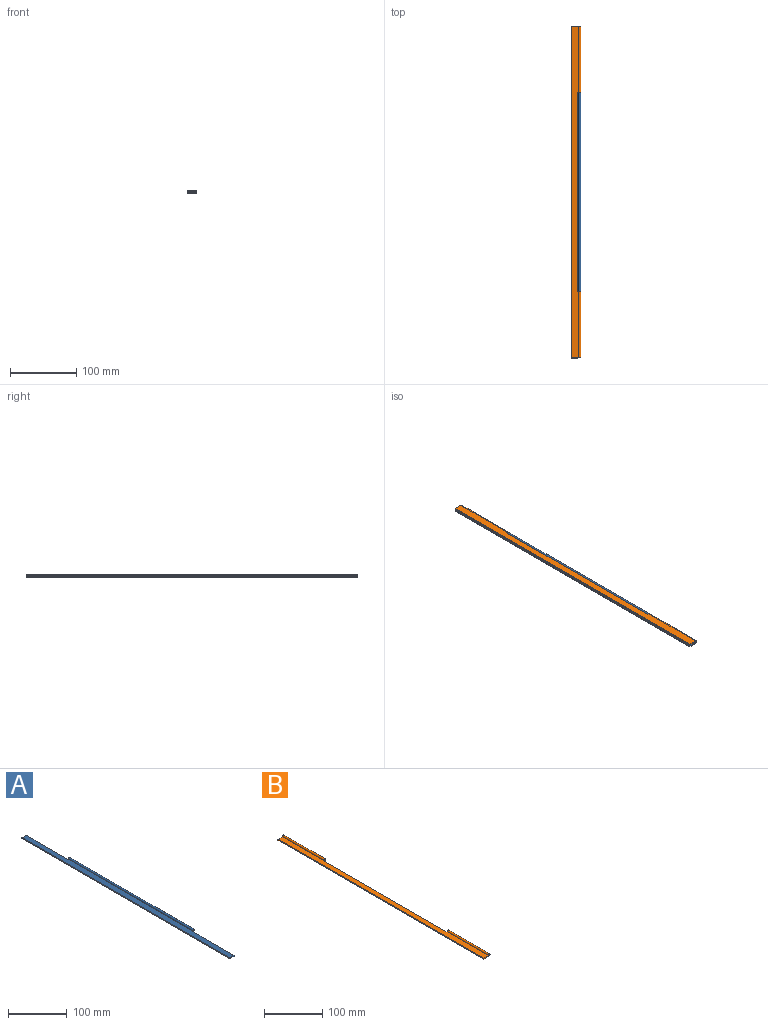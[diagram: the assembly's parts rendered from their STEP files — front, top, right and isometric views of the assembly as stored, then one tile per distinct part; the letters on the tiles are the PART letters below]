
ASSEMBLY  parts=2 mates=1
PART A: 12 faces, bbox 15x500x4.6 mm
  f0: plane 500x11.98mm, normal (0,0,-1), area 5594.8mm2, adj f1,f4,f5,f6,f7,f8,f9,f10
  f1: plane 300x0.84mm, normal (1,0,0), area 251.9mm2, adj f0,f2,f7,f9
  f2: cylinder r=2mm len=300mm, axis (0,1,0), area 3318.4mm2, adj f1,f3,f7,f9
  f3: plane 500x11.08mm, normal (0,0,1), area 5324.1mm2, adj f2,f4,f5,f6,f7,f8,f9,f10
  f4: plane 500x2mm, normal (-1,0,0), area 1000mm2, adj f0,f3,f5,f6
  f5: plane 10x2mm, normal (0,-1,0), area 20mm2, adj f0,f3,f4,f10
  f6: plane 10x2mm, normal (0,1,0), area 20mm2, adj f0,f3,f4,f8
  f7: plane 5x4.56mm, normal (0,1,0), area 12.7mm2, adj f0,f1,f2,f3,f8,f11
  f8: plane 100x2mm, normal (1,0,0), area 200mm2, adj f0,f3,f6,f7
  f9: plane 5x4.56mm, normal (0,-1,0), area 12.7mm2, adj f0,f1,f2,f3,f10,f11
  f10: plane 100x2mm, normal (1,0,0), area 200mm2, adj f0,f3,f5,f9
  f11: cylinder r=1mm len=300mm, axis (0,1,0), area 1885mm2, adj f7,f9
PART B: 14 faces, bbox 15x500x4.6 mm
  f0: plane 100x0.84mm, normal (1,0,0), area 84mm2, adj f1,f5,f9,f11
  f1: cylinder r=2mm len=100mm, axis (0,1,0), area 1106.1mm2, adj f0,f2,f9,f11
  f2: plane 500x11.08mm, normal (0,0,1), area 5216.1mm2, adj f1,f4,f7,f9,f10,f11,f12,f13
  f3: cylinder r=1mm len=100mm, axis (0,1,0), area 628.3mm2, adj f9,f11
  f4: plane 500x2mm, normal (-1,0,0), area 1000mm2, adj f2,f5,f9,f10
  f5: plane 500x11.98mm, normal (0,0,-1), area 5396.5mm2, adj f0,f4,f6,f9,f10,f11,f12,f13
  f6: plane 100x0.84mm, normal (1,0,0), area 84mm2, adj f5,f7,f10,f12
  f7: cylinder r=2mm len=100mm, axis (0,1,0), area 1106.1mm2, adj f2,f6,f10,f12
  f8: cylinder r=1mm len=100mm, axis (0,1,0), area 628.3mm2, adj f10,f12
  f9: plane 15x4.56mm, normal (0,-1,0), area 32.7mm2, adj f0,f1,f2,f3,f4,f5
  f10: plane 15x4.56mm, normal (0,1,0), area 32.7mm2, adj f2,f4,f5,f6,f7,f8
  f11: plane 5x4.56mm, normal (0,1,0), area 12.7mm2, adj f0,f1,f2,f3,f5,f13
  f12: plane 5x4.56mm, normal (0,-1,0), area 12.7mm2, adj f2,f5,f6,f7,f8,f13
  f13: plane 300x2mm, normal (1,0,0), area 600mm2, adj f2,f5,f11,f12
PLACE A t=(-129.96,172.28,-64.32)mm
PLACE B rot(axis=(1,0,0),180deg) t=(-129.96,-327.72,-59.2)mm
MATE revolute B.f1 <-> A.f2  axis (0,1,0) through (-116.96,-227.72,-61.76)mm
